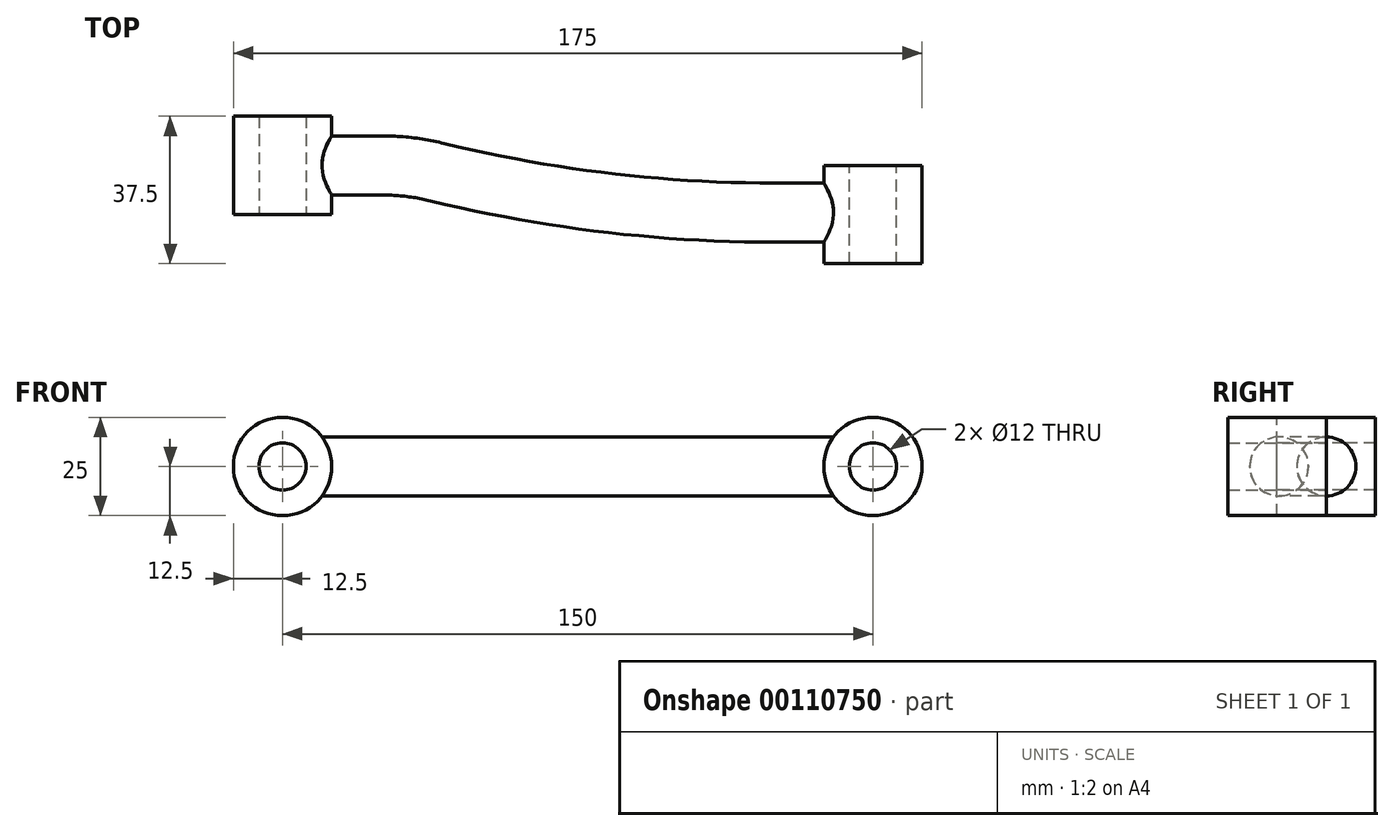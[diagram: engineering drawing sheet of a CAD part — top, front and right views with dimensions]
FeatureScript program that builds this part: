
annotation { "Feature Type Name" : "Feature", "Feature Type Description" : "" }
export const myFeature = defineFeature(function(context is Context, id is Id, definition is map)
    precondition{}
    {
        {
            var Q0;
            Q0=qCreatedBy(makeId("Front.planeOp"),FACE);
            var sketch = newSketch(context, id + "F0", { "sketchPlane" : qUnion([Q0])});
            skCircle(sketch, "E0", {"center": v(0, 0) * mm, "radius": 12.5 * mm});
            skCircle(sketch, "E1", {"center": v(0, 0) * mm, "radius": 6 * mm});
            skSolve(sketch);
        }
        {
            var Q0;
            Q0=makeQuery(id+"F0.imprint","IMPRINT",FACE,{"disambiguationData":[TD([[makeQuery(id+"F0.imprint","IMPRINT",EDGE,{"derivedFrom":sQuery(id+"F0.wireOp",EDGE,"E0")}),1.0]])]});
            extrude(context, id + "F1", {"entities" : qUnion([Q0]), "oppositeDirection" : true, "depth" : 25 * mm});
        }
        {
            var Q0;
            Q0=qCreatedBy(makeId("Front.planeOp"),FACE);
            var sketch = newSketch(context, id + "F2", { "sketchPlane" : qUnion([Q0])});
            skLineSegment(sketch, "E2", {"start": v(0, 0) * mm, "end": v(150, 0) * mm, "construction": true});
            skCircle(sketch, "E3", {"center": v(150, 0) * mm, "radius": 12.5 * mm});
            skCircle(sketch, "E4", {"center": v(150, 0) * mm, "radius": 6 * mm});
            skSolve(sketch);
        }
        {
            var Q0;
            Q0=makeQuery(id+"F2.imprint","IMPRINT",FACE,{"disambiguationData":[TD([[makeQuery(id+"F2.imprint","IMPRINT",EDGE,{"derivedFrom":sQuery(id+"F2.wireOp",EDGE,"E3")}),1.0]])]});
            extrude(context, id + "F3", {"entities" : qUnion([Q0]), "endBound" : BoundingType.SYMMETRIC, "depth" : 25 * mm});
        }
        {
            var Q0;
            Q0=qCreatedBy(makeId("Top.planeOp"),FACE);
            var sketch = newSketch(context, id + "F4", { "sketchPlane" : qUnion([Q0])});
            skLineSegment(sketch, "E5", {"start": v(0, 45.59) * mm, "end": v(0, -27.23) * mm, "construction": true});
            skLineSegment(sketch, "E6", {"start": v(0, 12) * mm, "end": v(25, 12) * mm});
            skArc(sketch, "E7", {"start": v(39.2, 10.3) * mm, "mid": v(32.15, 11.57) * mm, "end": v(25, 12) * mm});
            skArc(sketch, "E8", {"start": v(39.2, 10.3) * mm, "mid": v(81.79, 2.58) * mm, "end": v(125, 0) * mm});
            skLineSegment(sketch, "E9", {"start": v(150, 26.28) * mm, "end": v(150, -39.39) * mm, "construction": true});
            skLineSegment(sketch, "E10", {"start": v(125, 0) * mm, "end": v(150, 0) * mm});
            skSolve(sketch);
        }
        {
            var Q0;
            Q0=qCreatedBy(makeId("Right.planeOp"),FACE);
            var sketch = newSketch(context, id + "F5", { "sketchPlane" : qUnion([Q0])});
            skCircle(sketch, "E11", {"center": v(12.5, 0) * mm, "radius": 7.5 * mm});
            skSolve(sketch);
        }
        {
            var Q0;
            Q0 = qSketchRegion(id + "F5", true);
            var Q1;
            Q1=sQuery(id+"F4.wireOp",EDGE,"E8");
            var Q2;
            Q2=sQuery(id+"F4.wireOp",EDGE,"E7");
            var Q3;
            Q3=sQuery(id+"F4.wireOp",EDGE,"E6");
            var Q4;
            Q4=sQuery(id+"F4.wireOp",EDGE,"E10");
            sweep(context, id + "F6", {"operationType" : NewBodyOperationType.ADD, "profiles" : qUnion([Q0]), "path" : qUnion([Q1, Q2, Q3, Q4])});
        }
        {
            var Q0;
            Q0=makeQuery(id+"F0.imprint","IMPRINT",FACE,{"disambiguationData":[TD([[makeQuery(id+"F0.imprint","IMPRINT",EDGE,{"derivedFrom":sQuery(id+"F0.wireOp",EDGE,"E1")}),1.0]])]});
            var Q1;
            Q1=sQuery(id+"F0.wireOp",EDGE,"E1");
            extrude(context, id + "F7", {"entities" : qUnion([Q0]), "operationType" : NewBodyOperationType.REMOVE, "surfaceEntities" : qUnion([Q1]), "endBound" : BoundingType.THROUGH_ALL, "oppositeDirection" : true, "depth" : 25 * mm});
        }
        {
            var Q0;
            Q0=makeQuery(id+"F2.imprint","IMPRINT",FACE,{"disambiguationData":[TD([[makeQuery(id+"F2.imprint","IMPRINT",EDGE,{"derivedFrom":sQuery(id+"F2.wireOp",EDGE,"E4")}),1.0]])]});
            extrude(context, id + "F8", {"entities" : qUnion([Q0]), "operationType" : NewBodyOperationType.REMOVE, "endBound" : BoundingType.SYMMETRIC, "oppositeDirection" : true, "depth" : 50 * mm});
        }
    });
